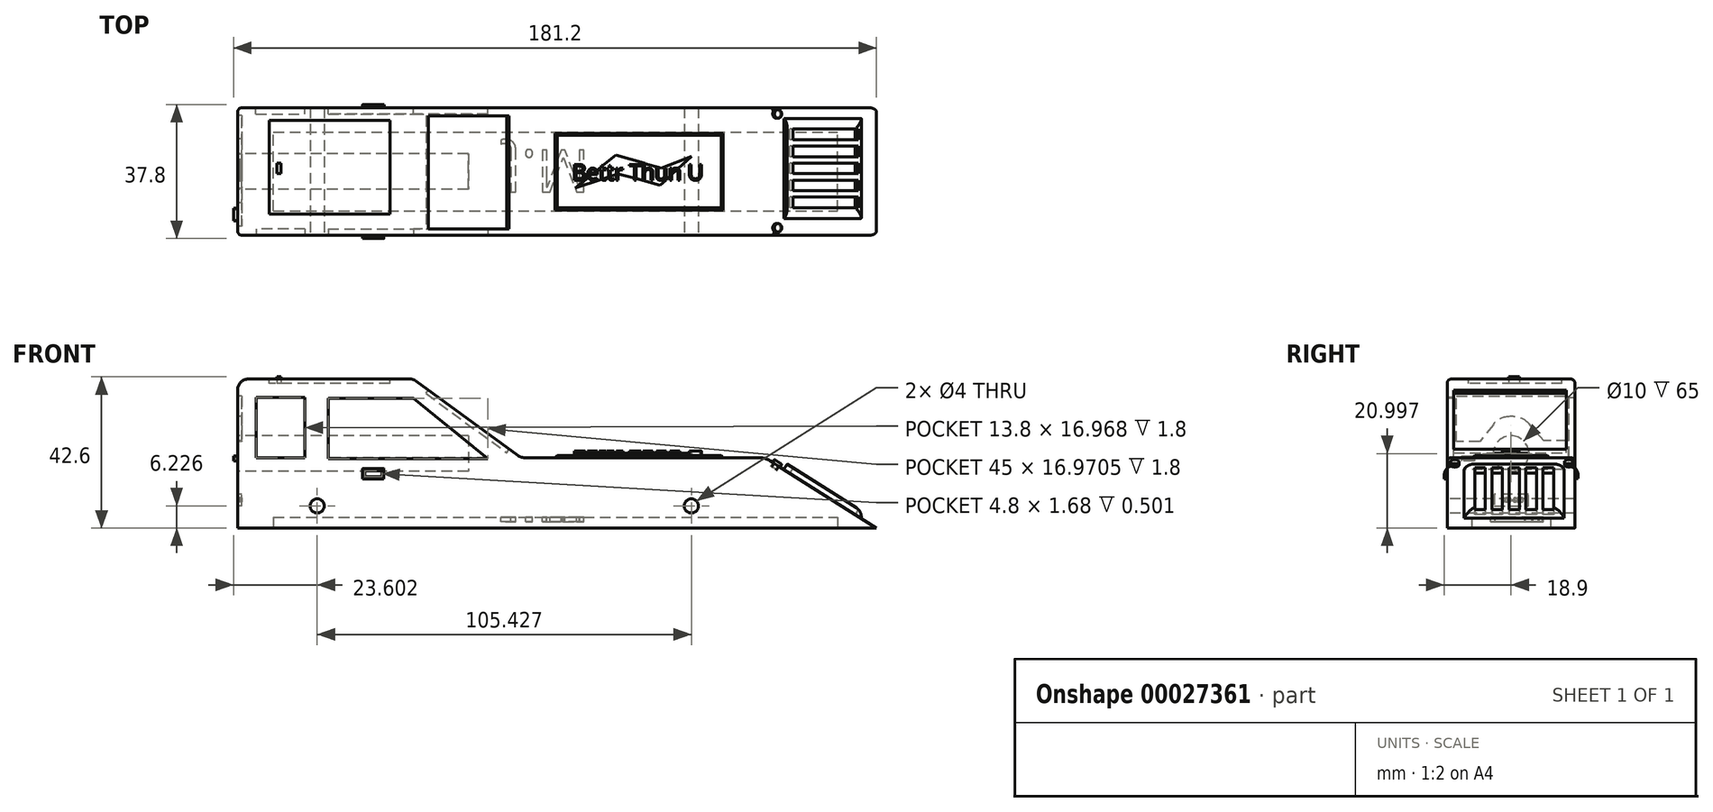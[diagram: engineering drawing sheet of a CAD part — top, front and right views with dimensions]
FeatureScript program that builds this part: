
annotation { "Feature Type Name" : "Feature", "Feature Type Description" : "" }
export const myFeature = defineFeature(function(context is Context, id is Id, definition is map)
    precondition{}
    {
        {
            var Q0;
            Q0=qCreatedBy(makeId("Front.planeOp"),FACE);
            var sketch = newSketch(context, id + "F0", { "sketchPlane" : qUnion([Q0])});
            skLineSegment(sketch, "E0.bottom", {"start": v(-82.47, -33.07) * mm, "end": v(217.53, -33.07) * mm});
            skLineSegment(sketch, "E0.left", {"start": v(-82.47, -33.07) * mm, "end": v(-82.47, 36.93) * mm});
            skLineSegment(sketch, "E1", {"start": v(217.53, -33.07) * mm, "end": v(165.18, 0) * mm});
            skLineSegment(sketch, "E2", {"start": v(165.18, 0) * mm, "end": v(50.43, 0) * mm});
            skLineSegment(sketch, "E3", {"start": v(50.43, 0) * mm, "end": v(0, 36.93) * mm});
            skLineSegment(sketch, "E4", {"start": v(0, 36.93) * mm, "end": v(-82.47, 36.93) * mm});
            skSolve(sketch);
        }
        {
            var Q0;
            Q0=makeQuery(id+"F0.imprint","IMPRINT",FACE,{"disambiguationData":[TD([[makeQuery(id+"F0.imprint","IMPRINT",EDGE,{"derivedFrom":sQuery(id+"F0.wireOp",EDGE,"E0.bottom")}),1.0]])]});
            extrude(context, id + "F1", {"entities" : qUnion([Q0]), "depth" : 60 * mm});
        }
        {
            var Q0;
            Q0=makeQuery(id+"F1.opExtrude","SWEPT_FACE",FACE,{"disambiguationData":[OSD([sQuery(id+"F0.wireOp",EDGE,"E0.left")])]});
            var sketch = newSketch(context, id + "F2", { "sketchPlane" : qUnion([Q0])});
            skCircle(sketch, "E5", {"center": v(30, 1.93) * mm, "radius": 5 * mm});
            skSolve(sketch);
        }
        {
            var Q0;
            Q0=makeQuery(id+"F2.imprint","IMPRINT",FACE,{"disambiguationData":[TD([[makeQuery(id+"F2.imprint","IMPRINT",EDGE,{"derivedFrom":sQuery(id+"F2.wireOp",EDGE,"E5")}),1.0]])]});
            extrude(context, id + "F3", {"entities" : qUnion([Q0]), "operationType" : NewBodyOperationType.REMOVE, "oppositeDirection" : true, "depth" : 65 * mm});
        }
        {
            var Q0;
            Q0=makeQuery(id+"F1.opExtrude","SWEPT_EDGE",EDGE,{"disambiguationData":[OSD([sQuery(id+"F0.wireOp",EDGE,"E1"),sQuery(id+"F0.wireOp",EDGE,"E2")])]});
            fillet(context, id + "F4", {"entities" : qUnion([Q0]), "radius" : 10 * mm, "tangentPropagation" : true, "allowEdgeOverflow" : false});
        }
        {
            var Q0;
            Q0=makeQuery(id+"F1.opExtrude","SWEPT_EDGE",EDGE,{"disambiguationData":[OSD([sQuery(id+"F0.wireOp",EDGE,"E2"),sQuery(id+"F0.wireOp",EDGE,"E3")])]});
            var Q1;
            Q1=makeQuery(id+"F1.opExtrude","SWEPT_EDGE",EDGE,{"disambiguationData":[OSD([sQuery(id+"F0.wireOp",EDGE,"E3"),sQuery(id+"F0.wireOp",EDGE,"E4")])]});
            fillet(context, id + "F5", {"entities" : qUnion([Q0, Q1]), "radius" : 5 * mm, "tangentPropagation" : true, "allowEdgeOverflow" : false});
        }
        {
            var Q0;
            Q0=makeQuery(id+"F1.opExtrude","CAP_FACE",FACE,{"disambiguationData":[OSD([sQuery(id+"F0.wireOp",EDGE,"E0.bottom"),sQuery(id+"F0.wireOp",EDGE,"E0.left"),sQuery(id+"F0.wireOp",EDGE,"E1"),sQuery(id+"F0.wireOp",EDGE,"E2"),sQuery(id+"F0.wireOp",EDGE,"E3"),sQuery(id+"F0.wireOp",EDGE,"E4")])],"isStart":false});
            var sketch = newSketch(context, id + "F6", { "sketchPlane" : qUnion([Q0])});
            skLineSegment(sketch, "E6", {"start": v(0, 27.87) * mm, "end": v(0, 27.87) * mm});
            skLineSegment(sketch, "E7", {"start": v(-40, -0.41) * mm, "end": v(-40, 27.87) * mm});
            skLineSegment(sketch, "E8", {"start": v(-40, 27.87) * mm, "end": v(0, 27.87) * mm});
            skLineSegment(sketch, "E9", {"start": v(-40, -0.41) * mm, "end": v(35, -0.41) * mm});
            skLineSegment(sketch, "E10", {"start": v(35, -0.41) * mm, "end": v(0, 27.87) * mm});
            skLineSegment(sketch, "E11", {"start": v(-73.89, 28.28) * mm, "end": v(-73.89, 0) * mm});
            skLineSegment(sketch, "E12", {"start": v(-50.89, 0) * mm, "end": v(-50.89, 28.28) * mm});
            skLineSegment(sketch, "E13", {"start": v(-50.89, 28.28) * mm, "end": v(-73.89, 28.28) * mm});
            skLineSegment(sketch, "E14", {"start": v(-73.89, 0) * mm, "end": v(-50.89, 0) * mm});
            skSolve(sketch);
        }
        {
            var Q0;
            Q0 = qSketchRegion(id + "F6", true);
            extrude(context, id + "F7", {"entities" : qUnion([Q0]), "operationType" : NewBodyOperationType.REMOVE, "oppositeDirection" : true, "depth" : 3 * mm});
        }
        {
            var Q0;
            Q0=makeQuery(id+"F1.opExtrude","CAP_FACE",FACE,{"disambiguationData":[OSD([sQuery(id+"F0.wireOp",EDGE,"E0.bottom"),sQuery(id+"F0.wireOp",EDGE,"E0.left"),sQuery(id+"F0.wireOp",EDGE,"E1"),sQuery(id+"F0.wireOp",EDGE,"E2"),sQuery(id+"F0.wireOp",EDGE,"E3"),sQuery(id+"F0.wireOp",EDGE,"E4")])],"isStart":true});
            var sketch = newSketch(context, id + "F8", { "sketchPlane" : qUnion([Q0])});
            skLineSegment(sketch, "E15", {"start": v(0, 28.28) * mm, "end": v(-35, 0) * mm});
            skLineSegment(sketch, "E16", {"start": v(-35, 0) * mm, "end": v(40, 0) * mm});
            skLineSegment(sketch, "E17", {"start": v(40, 0) * mm, "end": v(40, 28.28) * mm});
            skLineSegment(sketch, "E18", {"start": v(40, 28.28) * mm, "end": v(0, 28.28) * mm});
            skLineSegment(sketch, "E19", {"start": v(51, 28.28) * mm, "end": v(51, 0) * mm});
            skLineSegment(sketch, "E20", {"start": v(51, 0) * mm, "end": v(74, 0) * mm});
            skLineSegment(sketch, "E21", {"start": v(74, 0) * mm, "end": v(74, 28.28) * mm});
            skLineSegment(sketch, "E22", {"start": v(74, 28.28) * mm, "end": v(51, 28.28) * mm});
            skSolve(sketch);
        }
        {
            var Q0;
            Q0 = qSketchRegion(id + "F8", true);
            extrude(context, id + "F9", {"entities" : qUnion([Q0]), "operationType" : NewBodyOperationType.REMOVE, "oppositeDirection" : true, "depth" : 3 * mm});
        }
        {
            var Q0;
            Q0=makeQuery(id+"F1.opExtrude","SWEPT_FACE",FACE,{"disambiguationData":[OSD([sQuery(id+"F0.wireOp",EDGE,"E3")])]});
            var sketch = newSketch(context, id + "F10", { "sketchPlane" : qUnion([Q0])});
            skLineSegment(sketch, "E23", {"start": v(-13, -56.94) * mm, "end": v(34, -56.94) * mm});
            skLineSegment(sketch, "E24", {"start": v(34, -56.94) * mm, "end": v(34, -3.94) * mm});
            skLineSegment(sketch, "E25", {"start": v(34, -3.94) * mm, "end": v(-13, -3.94) * mm});
            skLineSegment(sketch, "E26", {"start": v(-13, -3.94) * mm, "end": v(-13, -56.94) * mm});
            skSolve(sketch);
        }
        {
            var Q0;
            Q0 = qSketchRegion(id + "F10", true);
            extrude(context, id + "F11", {"entities" : qUnion([Q0]), "operationType" : NewBodyOperationType.REMOVE, "oppositeDirection" : true, "depth" : 2 * mm});
        }
        {
            var Q0;
            Q0=makeQuery(id+"F1.opExtrude","SWEPT_EDGE",EDGE,{"disambiguationData":[OSD([sQuery(id+"F0.wireOp",EDGE,"E0.left"),sQuery(id+"F0.wireOp",EDGE,"E4")])]});
            fillet(context, id + "F12", {"entities" : qUnion([Q0]), "radius" : 5 * mm, "tangentPropagation" : true, "allowEdgeOverflow" : false});
        }
        {
            var Q0;
            Q0=makeQuery(id+"F1.opExtrude","CAP_FACE",FACE,{"disambiguationData":[OSD([sQuery(id+"F0.wireOp",EDGE,"E0.bottom"),sQuery(id+"F0.wireOp",EDGE,"E0.left"),sQuery(id+"F0.wireOp",EDGE,"E1"),sQuery(id+"F0.wireOp",EDGE,"E2"),sQuery(id+"F0.wireOp",EDGE,"E3"),sQuery(id+"F0.wireOp",EDGE,"E4")])],"isStart":false});
            var sketch = newSketch(context, id + "F13", { "sketchPlane" : qUnion([Q0])});
            skLineSegment(sketch, "E27", {"start": v(-23.82, -5.07) * mm, "end": v(-13.82, -5.07) * mm});
            skLineSegment(sketch, "E28", {"start": v(-13.82, -5.07) * mm, "end": v(-13.82, -10.07) * mm});
            skLineSegment(sketch, "E29", {"start": v(-13.82, -10.07) * mm, "end": v(-23.82, -10.07) * mm});
            skLineSegment(sketch, "E30", {"start": v(-23.82, -10.07) * mm, "end": v(-23.82, -5.07) * mm});
            skLineSegment(sketch, "E31", {"start": v(-22.8, -6.15) * mm, "end": v(-22.8, -8.95) * mm});
            skLineSegment(sketch, "E32", {"start": v(-22.8, -8.95) * mm, "end": v(-14.8, -8.95) * mm});
            skLineSegment(sketch, "E33", {"start": v(-14.8, -8.95) * mm, "end": v(-14.8, -6.15) * mm});
            skLineSegment(sketch, "E34", {"start": v(-14.8, -6.15) * mm, "end": v(-22.8, -6.15) * mm});
            skSolve(sketch);
        }
        {
            var Q0;
            Q0 = qSketchRegion(id + "F13", true);
            extrude(context, id + "F14", {"entities" : qUnion([Q0]), "operationType" : NewBodyOperationType.ADD, "depth" : 1.5 * mm});
        }
        {
            var Q0;
            Q0=makeQuery(id+"F1.opExtrude","CAP_FACE",FACE,{"disambiguationData":[OSD([sQuery(id+"F0.wireOp",EDGE,"E0.bottom"),sQuery(id+"F0.wireOp",EDGE,"E0.left"),sQuery(id+"F0.wireOp",EDGE,"E1"),sQuery(id+"F0.wireOp",EDGE,"E2"),sQuery(id+"F0.wireOp",EDGE,"E3"),sQuery(id+"F0.wireOp",EDGE,"E4")])],"isStart":true});
            var sketch = newSketch(context, id + "F15", { "sketchPlane" : qUnion([Q0])});
            skLineSegment(sketch, "E35", {"start": v(13.79, -4.77) * mm, "end": v(13.79, -9.77) * mm});
            skLineSegment(sketch, "E36", {"start": v(13.79, -9.77) * mm, "end": v(23.79, -9.77) * mm});
            skLineSegment(sketch, "E37", {"start": v(23.79, -9.77) * mm, "end": v(23.79, -4.77) * mm});
            skLineSegment(sketch, "E38", {"start": v(23.79, -4.77) * mm, "end": v(13.79, -4.77) * mm});
            skLineSegment(sketch, "E39", {"start": v(14.77, -5.87) * mm, "end": v(14.77, -8.67) * mm});
            skLineSegment(sketch, "E40", {"start": v(14.77, -8.67) * mm, "end": v(22.77, -8.67) * mm});
            skLineSegment(sketch, "E41", {"start": v(22.77, -8.67) * mm, "end": v(22.77, -5.87) * mm});
            skLineSegment(sketch, "E42", {"start": v(22.77, -5.87) * mm, "end": v(14.77, -5.87) * mm});
            skSolve(sketch);
        }
        {
            var Q0;
            Q0 = qSketchRegion(id + "F15", true);
            extrude(context, id + "F16", {"entities" : qUnion([Q0]), "operationType" : NewBodyOperationType.ADD, "depth" : 1.5 * mm});
        }
        {
            var Q0;
            Q0=makeQuery(id+"F16.opExtrude","CAP_EDGE",EDGE,{"disambiguationData":[OSD([sQuery(id+"F15.wireOp",EDGE,"E38")])],"isStart":false});
            fillet(context, id + "F17", {"entities" : qUnion([Q0]), "radius" : 5 * mm, "tangentPropagation" : true, "allowEdgeOverflow" : false});
        }
        {
            var Q0;
            Q0=makeQuery(id+"F14.opExtrude","CAP_EDGE",EDGE,{"disambiguationData":[OSD([sQuery(id+"F13.wireOp",EDGE,"E27")])],"isStart":false});
            fillet(context, id + "F18", {"entities" : qUnion([Q0]), "radius" : 5 * mm, "tangentPropagation" : true, "allowEdgeOverflow" : false});
        }
        {
            var Q0;
            Q0=makeQuery(id+"F1.opExtrude","SWEPT_FACE",FACE,{"disambiguationData":[OSD([sQuery(id+"F0.wireOp",EDGE,"E0.left")])]});
            var sketch = newSketch(context, id + "F19", { "sketchPlane" : qUnion([Q0])});
            skLineSegment(sketch, "E43", {"start": v(3.67, 28.92) * mm, "end": v(3.67, 7.92) * mm});
            skLineSegment(sketch, "E44", {"start": v(3.67, 7.92) * mm, "end": v(14.67, 7.92) * mm});
            skLineSegment(sketch, "E45", {"start": v(14.67, 7.92) * mm, "end": v(21.44, 15.81) * mm});
            skLineSegment(sketch, "E46", {"start": v(29.03, 19.3) * mm, "end": v(30.56, 19.3) * mm});
            skLineSegment(sketch, "E47", {"start": v(38.43, 15.46) * mm, "end": v(44.67, 7.49) * mm});
            skLineSegment(sketch, "E48", {"start": v(44.67, 7.49) * mm, "end": v(55.67, 7.49) * mm});
            skLineSegment(sketch, "E49", {"start": v(55.67, 7.49) * mm, "end": v(55.67, 28.92) * mm});
            skLineSegment(sketch, "E50", {"start": v(55.67, 28.92) * mm, "end": v(3.67, 28.92) * mm});
            skPoint(sketch, "E51.visualSharp", {"position": v(24.43, 19.3) * mm});
            skArc(sketch, "E51.filletArc", {"start": v(29.03, 19.3) * mm, "mid": v(24.85, 18.4) * mm, "end": v(21.44, 15.81) * mm});
            skPoint(sketch, "E52.visualSharp", {"position": v(35.43, 19.3) * mm});
            skArc(sketch, "E52.filletArc", {"start": v(38.43, 15.46) * mm, "mid": v(34.94, 18.3) * mm, "end": v(30.56, 19.3) * mm});
            skLineSegment(sketch, "E53", {"start": v(16.08, 9.56) * mm, "end": v(15.58, 8.97) * mm});
            skLineSegment(sketch, "E54", {"start": v(21.84, -17.18) * mm, "end": v(37.84, -17.18) * mm});
            skLineSegment(sketch, "E55", {"start": v(37.84, -17.18) * mm, "end": v(37.84, -22.68) * mm});
            skLineSegment(sketch, "E56", {"start": v(37.84, -22.68) * mm, "end": v(21.84, -22.68) * mm});
            skLineSegment(sketch, "E57", {"start": v(21.84, -22.68) * mm, "end": v(21.84, -17.18) * mm});
            skText(sketch, "E58", { "text": "062-002", "fontName": "OpenSans-Regular.ttf"});
            const initialGuessF19  = {"E58": [0.0242, -0.02085, 1, 0, 0.002]};
            skSetInitialGuess(sketch, initialGuessF19);
            skSolve(sketch);
        }
        {
            var Q0;
            Q0=makeQuery(id+"F1.opExtrude","SWEPT_FACE",FACE,{"disambiguationData":[OSD([sQuery(id+"F0.wireOp",EDGE,"E1")])]});
            var sketch = newSketch(context, id + "F20", { "sketchPlane" : qUnion([Q0])});
            skLineSegment(sketch, "E59", {"start": v(150.04, -5.03) * mm, "end": v(150.04, -52.03) * mm});
            skLineSegment(sketch, "E60", {"start": v(150.04, -52.03) * mm, "end": v(193.04, -52.03) * mm});
            skLineSegment(sketch, "E61", {"start": v(193.04, -52.03) * mm, "end": v(193.04, -5.03) * mm});
            skLineSegment(sketch, "E62", {"start": v(193.04, -5.03) * mm, "end": v(150.04, -5.03) * mm});
            skLineSegment(sketch, "E63", {"start": v(153.34, -10.03) * mm, "end": v(189.74, -10.03) * mm});
            skLineSegment(sketch, "E64", {"start": v(189.74, -10.03) * mm, "end": v(189.74, -15.03) * mm});
            skLineSegment(sketch, "E65", {"start": v(189.74, -15.03) * mm, "end": v(153.34, -15.03) * mm});
            skLineSegment(sketch, "E66", {"start": v(153.34, -15.03) * mm, "end": v(153.34, -10.03) * mm});
            skLineSegment(sketch, "E67", {"start": v(153.34, -18.03) * mm, "end": v(189.74, -18.03) * mm});
            skLineSegment(sketch, "E68", {"start": v(189.74, -18.03) * mm, "end": v(189.74, -23.03) * mm});
            skLineSegment(sketch, "E69", {"start": v(189.74, -23.03) * mm, "end": v(153.34, -23.03) * mm});
            skLineSegment(sketch, "E70", {"start": v(153.34, -23.03) * mm, "end": v(153.34, -18.03) * mm});
            skLineSegment(sketch, "E71", {"start": v(153.34, -26.03) * mm, "end": v(189.74, -26.03) * mm});
            skLineSegment(sketch, "E72", {"start": v(189.74, -26.03) * mm, "end": v(189.74, -31.03) * mm});
            skLineSegment(sketch, "E73", {"start": v(189.74, -31.03) * mm, "end": v(153.34, -31.03) * mm});
            skLineSegment(sketch, "E74", {"start": v(153.34, -31.03) * mm, "end": v(153.34, -26.03) * mm});
            skLineSegment(sketch, "E75", {"start": v(153.34, -34.03) * mm, "end": v(189.74, -34.03) * mm});
            skLineSegment(sketch, "E76", {"start": v(189.74, -34.03) * mm, "end": v(189.74, -39.03) * mm});
            skLineSegment(sketch, "E77", {"start": v(189.74, -39.03) * mm, "end": v(153.34, -39.03) * mm});
            skLineSegment(sketch, "E78", {"start": v(153.34, -39.03) * mm, "end": v(153.34, -34.03) * mm});
            skLineSegment(sketch, "E79", {"start": v(153.34, -42.03) * mm, "end": v(189.74, -42.03) * mm});
            skLineSegment(sketch, "E80", {"start": v(189.74, -42.03) * mm, "end": v(189.74, -47.03) * mm});
            skLineSegment(sketch, "E81", {"start": v(189.74, -47.03) * mm, "end": v(153.34, -47.03) * mm});
            skLineSegment(sketch, "E82", {"start": v(153.34, -47.03) * mm, "end": v(153.34, -42.03) * mm});
            skSolve(sketch);
        }
        {
            var Q0;
            Q0 = qSketchRegion(id + "F20", true);
            extrude(context, id + "F21", {"entities" : qUnion([Q0]), "operationType" : NewBodyOperationType.ADD, "depth" : 3 * mm});
        }
        {
            var Q0;
            Q0=makeQuery(id+"F21.opExtrude","CAP_EDGE",EDGE,{"disambiguationData":[OSD([sQuery(id+"F20.wireOp",EDGE,"E61")])],"isStart":false});
            var Q1;
            Q1=makeQuery(id+"F21.opExtrude","CAP_EDGE",EDGE,{"disambiguationData":[OSD([sQuery(id+"F20.wireOp",EDGE,"E60")])],"isStart":false});
            var Q2;
            Q2=makeQuery(id+"F21.opExtrude","CAP_EDGE",EDGE,{"disambiguationData":[OSD([sQuery(id+"F20.wireOp",EDGE,"E62")])],"isStart":false});
            fillet(context, id + "F22", {"entities" : qUnion([Q0, Q1, Q2]), "radius" : 5 * mm, "tangentPropagation" : true, "allowEdgeOverflow" : false});
        }
        {
            var Q0;
            Q0=makeQuery(id+"F1.opExtrude","SWEPT_FACE",FACE,{"disambiguationData":[OSD([sQuery(id+"F0.wireOp",EDGE,"E2")])]});
            var sketch = newSketch(context, id + "F23", { "sketchPlane" : qUnion([Q0])});
            skLineSegment(sketch, "E83", {"start": v(62.58, -8) * mm, "end": v(62.58, -52) * mm});
            skLineSegment(sketch, "E84", {"start": v(62.58, -52) * mm, "end": v(149.58, -52) * mm});
            skLineSegment(sketch, "E85", {"start": v(149.58, -52) * mm, "end": v(149.58, -8) * mm});
            skLineSegment(sketch, "E86", {"start": v(149.58, -8) * mm, "end": v(62.58, -8) * mm});
            skSolve(sketch);
        }
        {
            var Q0;
            Q0 = qSketchRegion(id + "F23", true);
            extrude(context, id + "F24", {"entities" : qUnion([Q0]), "operationType" : NewBodyOperationType.ADD, "depth" : 1 * mm});
        }
        {
            var Q0;
            Q0=makeQuery(id+"F24.opExtrude","CAP_EDGE",EDGE,{"disambiguationData":[OSD([sQuery(id+"F23.wireOp",EDGE,"E84")])],"isStart":false});
            var Q1;
            Q1=makeQuery(id+"F24.opExtrude","CAP_EDGE",EDGE,{"disambiguationData":[OSD([sQuery(id+"F23.wireOp",EDGE,"E85")])],"isStart":false});
            var Q2;
            Q2=makeQuery(id+"F24.opExtrude","CAP_EDGE",EDGE,{"disambiguationData":[OSD([sQuery(id+"F23.wireOp",EDGE,"E86")])],"isStart":false});
            var Q3;
            Q3=makeQuery(id+"F24.opExtrude","CAP_EDGE",EDGE,{"disambiguationData":[OSD([sQuery(id+"F23.wireOp",EDGE,"E83")])],"isStart":false});
            chamfer(context, id + "F25", {"entities" : qUnion([Q0, Q1, Q2, Q3]), "width" : 5 * mm, "tangentPropagation" : true});
        }
        {
            var Q0;
            Q0 = qSketchRegion(id + "F19", true);
            extrude(context, id + "F26", {"entities" : qUnion([Q0]), "operationType" : NewBodyOperationType.REMOVE, "oppositeDirection" : true, "depth" : 2 * mm});
        }
        {
            var Q0;
            Q0=makeQuery(id+"F1.opExtrude","SWEPT_FACE",FACE,{"disambiguationData":[OSD([sQuery(id+"F0.wireOp",EDGE,"E4")])]});
            var sketch = newSketch(context, id + "F27", { "sketchPlane" : qUnion([Q0])});
            skLineSegment(sketch, "E87", {"start": v(-67.65, -6.07) * mm, "end": v(-67.65, -49.96) * mm});
            skLineSegment(sketch, "E88", {"start": v(-67.65, -49.96) * mm, "end": v(-11.01, -49.96) * mm});
            skLineSegment(sketch, "E89", {"start": v(-11.01, -49.96) * mm, "end": v(-11.01, -6.07) * mm});
            skLineSegment(sketch, "E90", {"start": v(-11.01, -6.07) * mm, "end": v(-67.65, -6.07) * mm});
            skSolve(sketch);
        }
        {
            var Q0;
            Q0=makeQuery(id+"F27.imprint","IMPRINT",FACE,{"disambiguationData":[TD([[makeQuery(id+"F27.imprint","IMPRINT",EDGE,{"derivedFrom":sQuery(id+"F27.wireOp",EDGE,"E87")}),1.0]])]});
            extrude(context, id + "F28", {"entities" : qUnion([Q0]), "operationType" : NewBodyOperationType.REMOVE, "oppositeDirection" : true, "depth" : 2 * mm});
        }
        {
            var Q0;
            Q0=makeQuery(id+"F1.opExtrude","SWEPT_FACE",FACE,{"disambiguationData":[OSD([sQuery(id+"F0.wireOp",EDGE,"E0.left")])]});
            var sketch = newSketch(context, id + "F29", { "sketchPlane" : qUnion([Q0])});
            skLineSegment(sketch, "E91", {"start": v(47.24, 0.76) * mm, "end": v(47.24, -1.54) * mm});
            skLineSegment(sketch, "E92", {"start": v(47.24, -1.54) * mm, "end": v(53.14, -1.54) * mm});
            skLineSegment(sketch, "E93", {"start": v(53.14, -1.54) * mm, "end": v(53.14, 0.76) * mm});
            skLineSegment(sketch, "E94", {"start": v(53.14, 0.76) * mm, "end": v(47.24, 0.76) * mm});
            skLineSegment(sketch, "E95", {"start": v(47.87, 0) * mm, "end": v(47.87, -1.04) * mm});
            skLineSegment(sketch, "E96", {"start": v(47.87, -1.04) * mm, "end": v(52.6, -1.04) * mm});
            skLineSegment(sketch, "E97", {"start": v(52.6, -1.04) * mm, "end": v(52.6, 0) * mm});
            skLineSegment(sketch, "E98", {"start": v(52.6, 0) * mm, "end": v(47.87, 0) * mm});
            skSolve(sketch);
        }
        {
            var Q0;
            Q0 = qSketchRegion(id + "F29", true);
            extrude(context, id + "F30", {"entities" : qUnion([Q0]), "operationType" : NewBodyOperationType.ADD, "depth" : 2 * mm});
        }
        {
            var Q0;
            Q0=makeQuery(id+"F28.boolean.opBoolean","COPY",FACE,{"derivedFrom":makeQuery(id+"F28.opExtrude","CAP_FACE",FACE,{"disambiguationData":[OSD([sQuery(id+"F27.wireOp",EDGE,"E87"),sQuery(id+"F27.wireOp",EDGE,"E88"),sQuery(id+"F27.wireOp",EDGE,"E89"),sQuery(id+"F27.wireOp",EDGE,"E90")])],"isStart":false})});
            var sketch = newSketch(context, id + "F31", { "sketchPlane" : qUnion([Q0])});
            skLineSegment(sketch, "E99", {"start": v(-64.12, -26.05) * mm, "end": v(-64.12, -31.05) * mm});
            skLineSegment(sketch, "E100", {"start": v(-64.12, -31.05) * mm, "end": v(-62.12, -31.05) * mm});
            skLineSegment(sketch, "E101", {"start": v(-62.12, -31.05) * mm, "end": v(-62.12, -26.05) * mm});
            skLineSegment(sketch, "E102", {"start": v(-62.12, -26.05) * mm, "end": v(-64.12, -26.05) * mm});
            skSolve(sketch);
        }
        {
            var Q0;
            Q0 = qSketchRegion(id + "F31", true);
            extrude(context, id + "F32", {"entities" : qUnion([Q0]), "operationType" : NewBodyOperationType.ADD, "depth" : 3 * mm});
        }
        {
            var Q0;
            {var subQ0=sQuery(id+"F0.wireOp",EDGE,"E1");var subQ1=sQuery(id+"F0.wireOp",EDGE,"E0.bottom");Q0=makeQuery(id+"F21.boolean.opBoolean","SPLIT",FACE,{"disambiguationData":[TD([makeQuery(id+"F1.opExtrude","SWEPT_FACE",FACE,{"disambiguationData":[OSD([subQ1])]})])],"derivedFrom":makeQuery(id+"F1.opExtrude","SWEPT_FACE",FACE,{"disambiguationData":[OSD([subQ0])]})});}
            var sketch = newSketch(context, id + "F33", { "sketchPlane" : qUnion([Q0])});
            skCircle(sketch, "E103", {"center": v(145.91, -56.44) * mm, "radius": 2 * mm});
            skCircle(sketch, "E104", {"center": v(145.91, -2.94) * mm, "radius": 2 * mm});
            skSolve(sketch);
        }
        {
            var Q0;
            Q0 = qSketchRegion(id + "F33", true);
            extrude(context, id + "F34", {"entities" : qUnion([Q0]), "operationType" : NewBodyOperationType.ADD, "depth" : 1.6 * mm});
        }
        {
            var Q0;
            Q0=makeQuery(id+"F1.opExtrude","SWEPT_FACE",FACE,{"disambiguationData":[OSD([sQuery(id+"F0.wireOp",EDGE,"E0.bottom")])]});
            var sketch = newSketch(context, id + "F35", { "sketchPlane" : qUnion([Q0])});
            skLineSegment(sketch, "E105.bottom", {"start": v(-65.68, 48.5) * mm, "end": v(199.32, 48.5) * mm});
            skLineSegment(sketch, "E105.top", {"start": v(-65.68, 11.5) * mm, "end": v(199.32, 11.5) * mm});
            skLineSegment(sketch, "E105.right", {"start": v(199.32, 48.5) * mm, "end": v(199.32, 11.5) * mm});
            skLineSegment(sketch, "E106", {"start": v(-65.68, 48.5) * mm, "end": v(-65.68, 11.5) * mm});
            skSolve(sketch);
        }
        {
            var Q0;
            Q0 = qSketchRegion(id + "F35", true);
            extrude(context, id + "F36", {"entities" : qUnion([Q0]), "operationType" : NewBodyOperationType.REMOVE, "oppositeDirection" : true, "depth" : 5 * mm});
        }
        {
            var Q0;
            Q0=makeQuery(id+"F1.opExtrude","CAP_EDGE",EDGE,{"disambiguationData":[OSD([sQuery(id+"F0.wireOp",EDGE,"E2")])],"isStart":false});
            var Q1;
            Q1=makeQuery(id+"F1.opExtrude","CAP_EDGE",EDGE,{"disambiguationData":[OSD([sQuery(id+"F0.wireOp",EDGE,"E3")])],"isStart":false});
            var Q2;
            Q2=makeQuery(id+"F1.opExtrude","CAP_EDGE",EDGE,{"disambiguationData":[OSD([sQuery(id+"F0.wireOp",EDGE,"E4")])],"isStart":false});
            var Q3;
            Q3=makeQuery(id+"F1.opExtrude","CAP_EDGE",EDGE,{"disambiguationData":[OSD([sQuery(id+"F0.wireOp",EDGE,"E2")])],"isStart":true});
            fillet(context, id + "F37", {"entities" : qUnion([Q0, Q1, Q2, Q3]), "radius" : 2 * mm, "tangentPropagation" : true, "allowEdgeOverflow" : false});
        }
        {
            var Q0;
            Q0=makeQuery(id+"F24.opExtrude","CAP_FACE",FACE,{"disambiguationData":[OSD([sQuery(id+"F23.wireOp",EDGE,"E83"),sQuery(id+"F23.wireOp",EDGE,"E84"),sQuery(id+"F23.wireOp",EDGE,"E85"),sQuery(id+"F23.wireOp",EDGE,"E86")])],"isStart":false});
            var sketch = newSketch(context, id + "F38", { "sketchPlane" : qUnion([Q0])});
            skText(sketch, "E107", { "text": "Bettr Thun U", "fontName": "OpenSans-Regular.ttf"});
            const initialGuessF38  = {"E107": [0.07456, -0.03404, 1, 0, 0.00745]};
            skSetInitialGuess(sketch, initialGuessF38);
            skSolve(sketch);
        }
        {
            var Q0;
            Q0 = qSketchRegion(id + "F38", true);
            extrude(context, id + "F39", {"entities" : qUnion([Q0]), "operationType" : NewBodyOperationType.ADD, "depth" : 2 * mm});
        }
        {
            var Q0;
            {var subQ0=sQuery(id+"F23.wireOp",EDGE,"E83");var subQ1=sQuery(id+"F23.wireOp",EDGE,"E84");var subQ2=sQuery(id+"F23.wireOp",EDGE,"E85");var subQ3=sQuery(id+"F23.wireOp",EDGE,"E86");Q0=makeQuery(id+"F39.boolean.opBoolean","SPLIT",FACE,{"disambiguationData":[TD([makeQuery(id+"F25.opChamfer","BLEND_FACE",FACE,{"disambiguationData":[OSD([subQ0])]})])],"derivedFrom":makeQuery(id+"F24.opExtrude","CAP_FACE",FACE,{"disambiguationData":[OSD([subQ0,subQ1,subQ2,subQ3])],"isStart":false})});}
            var sketch = newSketch(context, id + "F40", { "sketchPlane" : qUnion([Q0])});
            skLineSegment(sketch, "E108", {"start": v(76.12, -37.77) * mm, "end": v(95.2, -22.21) * mm});
            skLineSegment(sketch, "E109", {"start": v(95.2, -22.21) * mm, "end": v(116.5, -28.5) * mm});
            skLineSegment(sketch, "E110", {"start": v(116.5, -28.5) * mm, "end": v(130.59, -22.95) * mm});
            skLineSegment(sketch, "E111", {"start": v(130.59, -22.95) * mm, "end": v(115.9, -36.45) * mm});
            skLineSegment(sketch, "E112", {"start": v(115.9, -36.45) * mm, "end": v(96.11, -31.07) * mm});
            skLineSegment(sketch, "E113", {"start": v(96.11, -31.07) * mm, "end": v(76.12, -37.77) * mm});
            skSolve(sketch);
        }
        {
            var Q0;
            Q0 = qSketchRegion(id + "F40", true);
            extrude(context, id + "F41", {"entities" : qUnion([Q0]), "operationType" : NewBodyOperationType.ADD, "depth" : 1 * mm});
        }
        {
            var Q0;
            Q0=makeQuery(id+"F36.boolean.opBoolean","COPY",FACE,{"derivedFrom":makeQuery(id+"F36.opExtrude","CAP_FACE",FACE,{"disambiguationData":[OSD([sQuery(id+"F35.wireOp",EDGE,"E105.bottom"),sQuery(id+"F35.wireOp",EDGE,"E105.top"),sQuery(id+"F35.wireOp",EDGE,"E105.right"),sQuery(id+"F35.wireOp",EDGE,"E106")])],"isStart":false})});
            var sketch = newSketch(context, id + "F42", { "sketchPlane" : qUnion([Q0])});
            skText(sketch, "E114", { "text": "J.M", "fontName": "OpenSans-Regular.ttf"});
            const initialGuessF42  = {"E114": [0.04333, 0.02004, 1, 0, 0.01982]};
            skSetInitialGuess(sketch, initialGuessF42);
            skSolve(sketch);
        }
        {
            var Q0;
            Q0 = qSketchRegion(id + "F42", true);
            extrude(context, id + "F43", {"entities" : qUnion([Q0]), "operationType" : NewBodyOperationType.ADD, "depth" : 2 * mm});
        }
        {
            var Q0;
            Q0=makeQuery(id+"F1.opExtrude","SWEPT_BODY",BODY,{"disambiguationData":[OSD([sQuery(id+"F0.wireOp",EDGE,"E0.bottom"),sQuery(id+"F0.wireOp",EDGE,"E0.left"),sQuery(id+"F0.wireOp",EDGE,"E1"),sQuery(id+"F0.wireOp",EDGE,"E2"),sQuery(id+"F0.wireOp",EDGE,"E3"),sQuery(id+"F0.wireOp",EDGE,"E4")])]});
            var Q1;
            {var subQ0=sQuery(id+"F0.wireOp",EDGE,"E2");var subQ1=sQuery(id+"F0.wireOp",EDGE,"E3");Q1=makeQuery(id+"F37.opFillet","BLEND_VERTEX",VERTEX,{"blendedFrom":[makeQuery(id+"F5.opFillet","BLEND_EDGE",EDGE,{"blendedFrom":[makeQuery(id+"F1.opExtrude","SWEPT_EDGE",EDGE,{"disambiguationData":[OSD([subQ0,subQ1])]}),makeQuery(id+"F1.opExtrude","CAP_FACE",FACE,{"disambiguationData":[OSD([sQuery(id+"F0.wireOp",EDGE,"E0.bottom"),sQuery(id+"F0.wireOp",EDGE,"E0.left"),sQuery(id+"F0.wireOp",EDGE,"E1"),subQ0,subQ1,sQuery(id+"F0.wireOp",EDGE,"E4")])],"isStart":false})],"blendedInto":[makeQuery(id+"F1.opExtrude","CAP_FACE",FACE,{"disambiguationData":[OSD([sQuery(id+"F0.wireOp",EDGE,"E0.bottom"),sQuery(id+"F0.wireOp",EDGE,"E0.left"),sQuery(id+"F0.wireOp",EDGE,"E1"),subQ0,subQ1,sQuery(id+"F0.wireOp",EDGE,"E4")])],"isStart":false})]}),makeQuery(id+"F1.opExtrude","CAP_EDGE",EDGE,{"disambiguationData":[OSD([subQ0])],"isStart":false}),makeQuery(id+"F5.opFillet","BLEND_FACE",FACE,{"disambiguationData":[OSD([subQ0,subQ1])]}),makeQuery(id+"F1.opExtrude","SWEPT_FACE",FACE,{"disambiguationData":[OSD([subQ0])]})],"blendedInto":[makeQuery(id+"F5.opFillet","BLEND_FACE",FACE,{"disambiguationData":[OSD([subQ0,subQ1])]}),makeQuery(id+"F1.opExtrude","SWEPT_FACE",FACE,{"disambiguationData":[OSD([subQ0])]})]});}
            transform(context, id + "F44", {"entities" : qUnion([Q0]), "transformType" : TransformType.SCALE_UNIFORMLY, "scale" : .6, "makeCopy" : false, "scalePoint" : qUnion([Q1])});
        }
        {
            var Q0;
            {var subQ0=sQuery(id+"F0.wireOp",EDGE,"E0.bottom");var subQ1=sQuery(id+"F0.wireOp",EDGE,"E0.left");var subQ2=sQuery(id+"F0.wireOp",EDGE,"E1");var subQ3=sQuery(id+"F0.wireOp",EDGE,"E2");var subQ4=sQuery(id+"F0.wireOp",EDGE,"E3");var subQ5=sQuery(id+"F0.wireOp",EDGE,"E4");Q0=makeQuery(id+"F14.boolean.opBoolean","SPLIT",FACE,{"disambiguationData":[TD([makeQuery(id+"F1.opExtrude","SWEPT_FACE",FACE,{"disambiguationData":[OSD([subQ0])]})])],"derivedFrom":makeQuery(id+"F1.opExtrude","CAP_FACE",FACE,{"disambiguationData":[OSD([subQ0,subQ1,subQ2,subQ3,subQ4,subQ5])],"isStart":false})});}
            var sketch = newSketch(context, id + "F45", { "sketchPlane" : qUnion([Q0])});
            skCircle(sketch, "E115", {"center": v(-6.26, -13.61) * mm, "radius": 2 * mm});
            skCircle(sketch, "E116", {"center": v(99.17, -13.61) * mm, "radius": 2 * mm});
            skSolve(sketch);
        }
        {
            var Q0;
            Q0 = qSketchRegion(id + "F45", true);
            extrude(context, id + "F46", {"entities" : qUnion([Q0]), "operationType" : NewBodyOperationType.REMOVE, "endBound" : BoundingType.THROUGH_ALL, "oppositeDirection" : true, "depth" : 25 * mm});
        }
        {
            var Q0;
            {var subQ0=sQuery(id+"F0.wireOp",EDGE,"E0.left");var subQ17=sQuery(id+"F0.wireOp",EDGE,"E0.bottom");var subQ24=makeQuery(id+"F1.opExtrude","SWEPT_FACE",FACE,{"disambiguationData":[OSD([subQ17])]});Q0=makeQuery(id+"F30.boolean.opBoolean","SPLIT",FACE,{"disambiguationData":[TD([subQ24])],"derivedFrom":makeQuery(id+"F26.boolean.opBoolean","SPLIT",FACE,{"disambiguationData":[TD([subQ24])],"derivedFrom":makeQuery(id+"F1.opExtrude","SWEPT_FACE",FACE,{"disambiguationData":[OSD([subQ0])]})})});}
            var sketch = newSketch(context, id + "F47", { "sketchPlane" : qUnion([Q0])});
            skCircle(sketch, "E117", {"center": v(41.2, 1.16) * mm, "radius": 5 * mm});
            skSolve(sketch);
        }
        {
            var Q0;
            Q0 = qSketchRegion(id + "F47", true);
            extrude(context, id + "F48", {"entities" : qUnion([Q0]), "operationType" : NewBodyOperationType.REMOVE, "oppositeDirection" : true, "depth" : 65 * mm});
        }
    });
